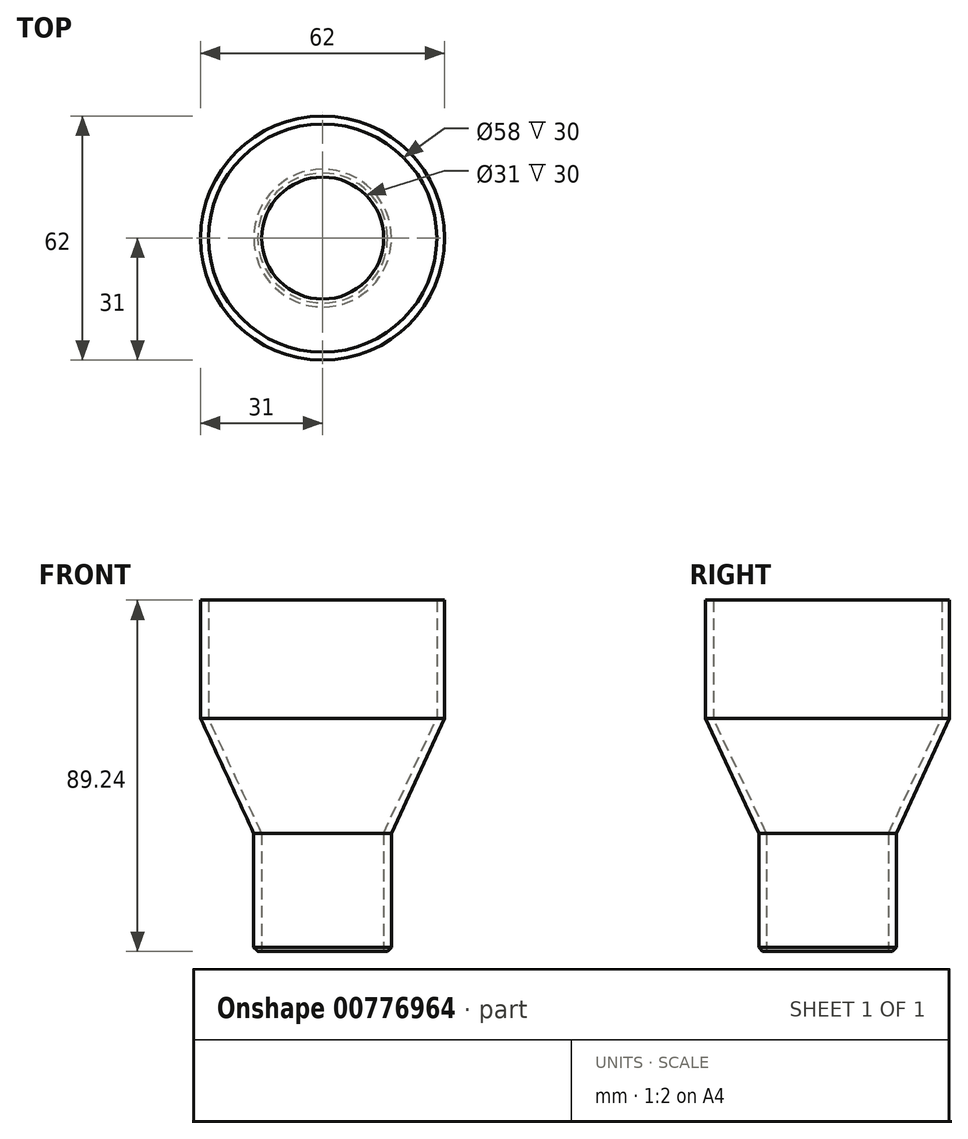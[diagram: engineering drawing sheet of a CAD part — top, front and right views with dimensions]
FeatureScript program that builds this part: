
annotation { "Feature Type Name" : "Feature", "Feature Type Description" : "" }
export const myFeature = defineFeature(function(context is Context, id is Id, definition is map)
    precondition{}
    {
        {
            var Q0;
            Q0=qCreatedBy(makeId("Front.planeOp"),FACE);
            var sketch = newSketch(context, id + "F0", { "sketchPlane" : qUnion([Q0])});
            skLineSegment(sketch, "E0.bottom", {"start": v(29, 51.35) * mm, "end": v(31, 51.35) * mm});
            skLineSegment(sketch, "E0.top", {"start": v(29, 21.35) * mm, "end": v(31, 21.35) * mm});
            skLineSegment(sketch, "E0.left", {"start": v(29, 51.35) * mm, "end": v(29, 21.35) * mm});
            skLineSegment(sketch, "E0.right", {"start": v(31, 51.35) * mm, "end": v(31, 21.35) * mm});
            skLineSegment(sketch, "E1.bottom", {"start": v(15.5, -7.89) * mm, "end": v(17.5, -7.89) * mm});
            skLineSegment(sketch, "E1.top", {"start": v(15.5, -37.89) * mm, "end": v(17.5, -37.89) * mm});
            skLineSegment(sketch, "E1.left", {"start": v(15.5, -7.89) * mm, "end": v(15.5, -37.89) * mm});
            skLineSegment(sketch, "E1.right", {"start": v(17.5, -7.89) * mm, "end": v(17.5, -37.89) * mm});
            skLineSegment(sketch, "E2", {"start": v(29, 21.35) * mm, "end": v(15.5, -7.89) * mm});
            skLineSegment(sketch, "E3", {"start": v(31, 21.35) * mm, "end": v(17.5, -7.89) * mm});
            skLineSegment(sketch, "E4", {"start": v(0, -23.58) * mm, "end": v(0, 49.51) * mm});
            skSolve(sketch);
        }
        {
            var Q0;
            Q0 = qSketchRegion(id + "F0", true);
            var Q1;
            Q1=sQuery(id+"F0.wireOp",EDGE,"E4");
            revolve(context, id + "F1", {"surfaceOperationType" : NewSurfaceOperationType.NEW, "entities" : qUnion([Q0]), "axis" : qUnion([Q1]), "revolveType" : RevolveType.FULL});
        }
        {
            var Q0;
            Q0=makeQuery(id+"F1.opRevolve","SWEPT_EDGE",EDGE,{"disambiguationData":[OSD([sQuery(id+"F0.wireOp",EDGE,"E1.top"),sQuery(id+"F0.wireOp",EDGE,"E1.right")])]});
            chamfer(context, id + "F2", {"entities" : qUnion([Q0]), "width" : 1 * mm, "tangentPropagation" : true});
        }
    });
